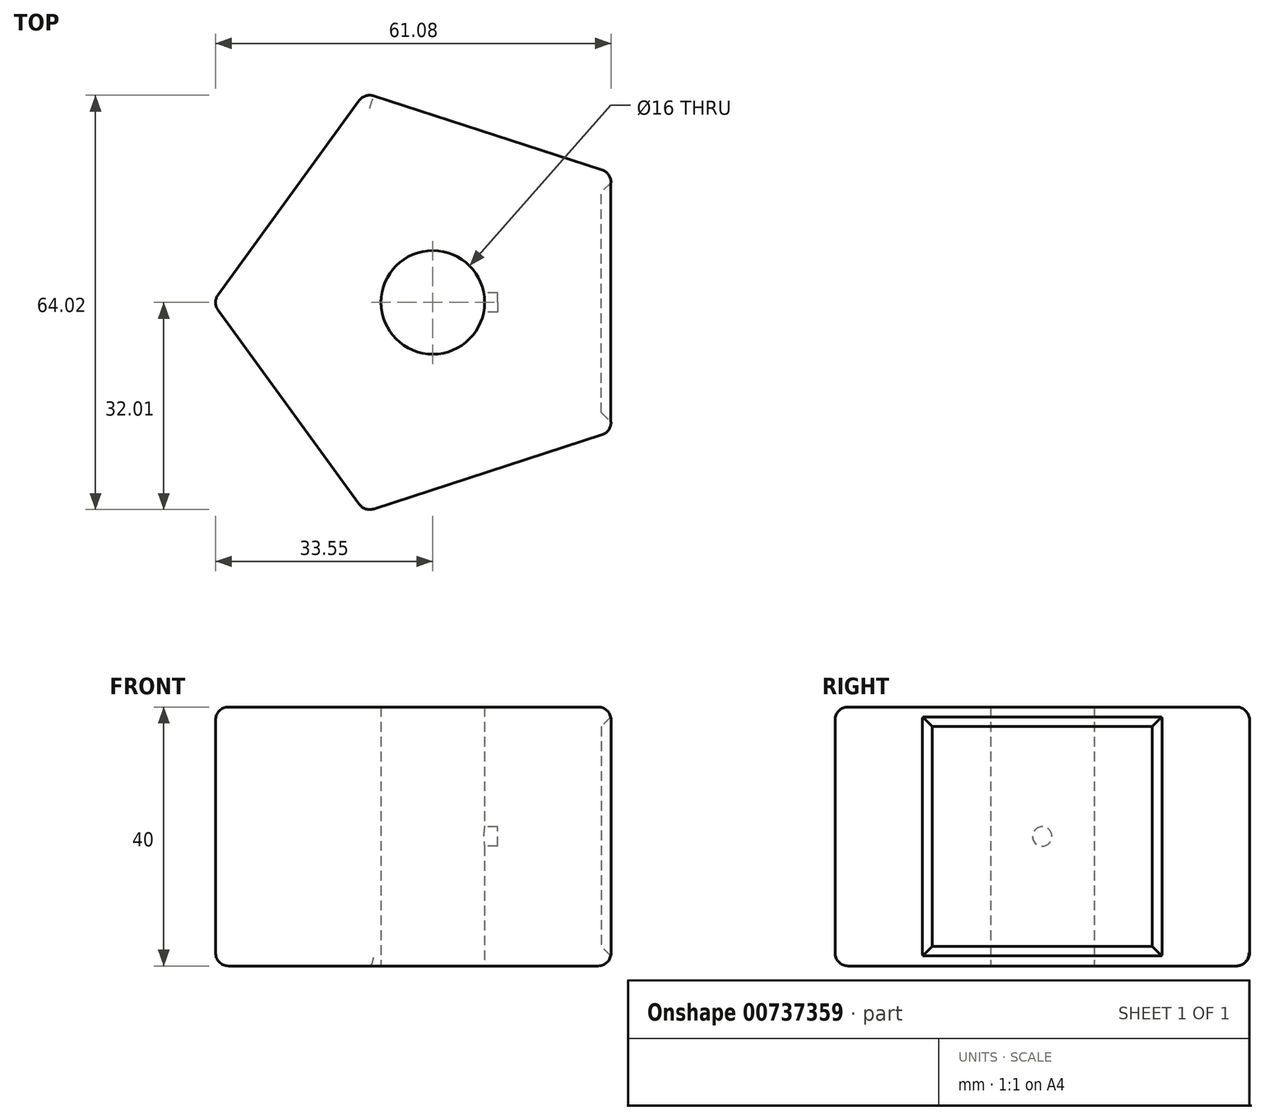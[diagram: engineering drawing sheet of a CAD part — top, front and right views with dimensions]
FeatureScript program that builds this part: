
annotation { "Feature Type Name" : "Feature", "Feature Type Description" : "" }
export const myFeature = defineFeature(function(context is Context, id is Id, definition is map)
    precondition{}
    {
        {
            var Q0;
            Q0=qCreatedBy(makeId("Top.planeOp"),FACE);
            var sketch = newSketch(context, id + "F0", { "sketchPlane" : qUnion([Q0])});
            skCircle(sketch, "E0.cCircle", {"center": v(0, 0) * mm, "radius": 27.53 * mm, "construction": true});
            skLineSegment(sketch, "E0.0", {"start": v(27.53, 20) * mm, "end": v(27.53, -20) * mm});
            skLineSegment(sketch, "E0.1", {"start": v(27.53, -20) * mm, "end": v(-10.51, -32.36) * mm});
            skLineSegment(sketch, "E0.2", {"start": v(-10.51, -32.36) * mm, "end": v(-34.03, 0) * mm});
            skLineSegment(sketch, "E0.3", {"start": v(-34.03, 0) * mm, "end": v(-10.51, 32.36) * mm});
            skLineSegment(sketch, "E0.4", {"start": v(-10.51, 32.36) * mm, "end": v(27.53, 20) * mm});
            skPoint(sketch, "E0.0.midPoint", {"position": v(27.53, 0) * mm});
            skCircle(sketch, "E1", {"center": v(0, 0) * mm, "radius": 8 * mm});
            skSolve(sketch);
        }
        {
            var Q0;
            Q0 = qSketchRegion(id + "F0", true);
            extrude(context, id + "F1", {"entities" : qUnion([Q0]), "depth" : 40 * mm, "offsetDistance" : 25 * mm});
        }
        {
            var Q0;
            Q0=makeQuery(id+"F1.opExtrude","SWEPT_FACE",FACE,{"disambiguationData":[OSD([sQuery(id+"F0.wireOp",EDGE,"E0.0")])]});
            var sketch = newSketch(context, id + "F2", { "sketchPlane" : qUnion([Q0])});
            skLineSegment(sketch, "E2.bottom", {"start": v(-18.5, 38.5) * mm, "end": v(18.5, 38.5) * mm});
            skLineSegment(sketch, "E2.top", {"start": v(-18.5, 1.5) * mm, "end": v(18.5, 1.5) * mm});
            skLineSegment(sketch, "E2.left", {"start": v(-18.5, 38.5) * mm, "end": v(-18.5, 1.5) * mm});
            skLineSegment(sketch, "E2.right", {"start": v(18.5, 38.5) * mm, "end": v(18.5, 1.5) * mm});
            skSolve(sketch);
        }
        {
            var Q0;
            Q0 = qSketchRegion(id + "F2", true);
            extrude(context, id + "F3", {"entities" : qUnion([Q0]), "operationType" : NewBodyOperationType.REMOVE, "oppositeDirection" : true, "depth" : 1.5 * mm, "offsetDistance" : 25 * mm});
        }
        {
            var Q0;
            Q0=makeQuery(id+"F3.boolean.opBoolean","COPY",FACE,{"derivedFrom":makeQuery(id+"F3.opExtrude","CAP_FACE",FACE,{"disambiguationData":[OSD([sQuery(id+"F2.wireOp",EDGE,"E2.bottom"),sQuery(id+"F2.wireOp",EDGE,"E2.top"),sQuery(id+"F2.wireOp",EDGE,"E2.left"),sQuery(id+"F2.wireOp",EDGE,"E2.right")])],"isStart":false})});
            var Q1;
            Q1=makeQuery(id+"FQoVGiJOBUNMoMP_1.-4.F3.boolean.opBoolean","COPY",FACE,{"derivedFrom":makeQuery(id+"FQoVGiJOBUNMoMP_1.-4.F3.opExtrude","CAP_FACE",FACE,{"disambiguationData":[OSD([sQuery(id+"F2.wireOp",EDGE,"E2.bottom"),sQuery(id+"F2.wireOp",EDGE,"E2.top"),sQuery(id+"F2.wireOp",EDGE,"E2.left"),sQuery(id+"F2.wireOp",EDGE,"E2.right")])],"isStart":false})});
            var Q2;
            Q2=makeQuery(id+"FQoVGiJOBUNMoMP_1.-3.F3.boolean.opBoolean","COPY",FACE,{"derivedFrom":makeQuery(id+"FQoVGiJOBUNMoMP_1.-3.F3.opExtrude","CAP_FACE",FACE,{"disambiguationData":[OSD([sQuery(id+"F2.wireOp",EDGE,"E2.bottom"),sQuery(id+"F2.wireOp",EDGE,"E2.top"),sQuery(id+"F2.wireOp",EDGE,"E2.left"),sQuery(id+"F2.wireOp",EDGE,"E2.right")])],"isStart":false})});
            var Q3;
            Q3=makeQuery(id+"FQoVGiJOBUNMoMP_1.-2.F3.boolean.opBoolean","COPY",FACE,{"derivedFrom":makeQuery(id+"FQoVGiJOBUNMoMP_1.-2.F3.opExtrude","CAP_FACE",FACE,{"disambiguationData":[OSD([sQuery(id+"F2.wireOp",EDGE,"E2.bottom"),sQuery(id+"F2.wireOp",EDGE,"E2.top"),sQuery(id+"F2.wireOp",EDGE,"E2.left"),sQuery(id+"F2.wireOp",EDGE,"E2.right")])],"isStart":false})});
            var Q4;
            Q4=makeQuery(id+"FQoVGiJOBUNMoMP_1.-1.F3.boolean.opBoolean","COPY",FACE,{"derivedFrom":makeQuery(id+"FQoVGiJOBUNMoMP_1.-1.F3.opExtrude","CAP_FACE",FACE,{"disambiguationData":[OSD([sQuery(id+"F2.wireOp",EDGE,"E2.bottom"),sQuery(id+"F2.wireOp",EDGE,"E2.top"),sQuery(id+"F2.wireOp",EDGE,"E2.left"),sQuery(id+"F2.wireOp",EDGE,"E2.right")])],"isStart":false})});
            chamfer(context, id + "F4", {"entities" : qUnion([Q0, Q1, Q2, Q3, Q4]), "width" : 1.5 * mm, "tangentPropagation" : true});
        }
        {
            var Q0;
            Q0=qCreatedBy(makeId("Right.planeOp"),FACE);
            var sketch = newSketch(context, id + "F5", { "sketchPlane" : qUnion([Q0])});
            skCircle(sketch, "E3", {"center": v(0, 49.5) * mm, "radius": 3 * mm});
            skSolve(sketch);
        }
        {
            var Q0;
            Q0 = qSketchRegion(id + "F5", true);
            extrude(context, id + "F6", {"entities" : qUnion([Q0]), "operationType" : NewBodyOperationType.REMOVE, "depth" : 20 * mm, "offsetDistance" : 25 * mm});
        }
        {
            var Q0;
            Q0=makeQuery(id+"F1.opExtrude","SWEPT_EDGE",EDGE,{"disambiguationData":[OSD([sQuery(id+"F0.wireOp",EDGE,"E0.2"),sQuery(id+"F0.wireOp",EDGE,"E0.3")])]});
            var Q1;
            Q1=makeQuery(id+"F1.opExtrude","SWEPT_EDGE",EDGE,{"disambiguationData":[OSD([sQuery(id+"F0.wireOp",EDGE,"E0.1"),sQuery(id+"F0.wireOp",EDGE,"E0.2")])]});
            var Q2;
            Q2=makeQuery(id+"F1.opExtrude","SWEPT_EDGE",EDGE,{"disambiguationData":[OSD([sQuery(id+"F0.wireOp",EDGE,"E0.0"),sQuery(id+"F0.wireOp",EDGE,"E0.1")])]});
            var Q3;
            Q3=makeQuery(id+"F1.opExtrude","SWEPT_EDGE",EDGE,{"disambiguationData":[OSD([sQuery(id+"F0.wireOp",EDGE,"E0.0"),sQuery(id+"F0.wireOp",EDGE,"E0.4")])]});
            var Q4;
            Q4=makeQuery(id+"F1.opExtrude","SWEPT_EDGE",EDGE,{"disambiguationData":[OSD([sQuery(id+"F0.wireOp",EDGE,"E0.3"),sQuery(id+"F0.wireOp",EDGE,"E0.4")])]});
            fillet(context, id + "F7", {"entities" : qUnion([Q0, Q1, Q2, Q3, Q4]), "radius" : 2 * mm, "tangentPropagation" : true, "allowEdgeOverflow" : false});
        }
        {
            var Q0;
            Q0=makeQuery(id+"F1.opExtrude","CAP_EDGE",EDGE,{"disambiguationData":[OSD([sQuery(id+"F0.wireOp",EDGE,"E0.1")])],"isStart":false});
            var Q1;
            Q1=makeQuery(id+"F1.opExtrude","CAP_EDGE",EDGE,{"disambiguationData":[OSD([sQuery(id+"F0.wireOp",EDGE,"E0.1")])],"isStart":true});
            fillet(context, id + "F8", {"entities" : qUnion([Q0, Q1]), "radius" : 2 * mm, "tangentPropagation" : true, "allowEdgeOverflow" : false});
        }
        {
            var Q0;
            Q0=qCreatedBy(makeId("Right.planeOp"),FACE);
            var sketch = newSketch(context, id + "F9", { "sketchPlane" : qUnion([Q0])});
            skCircle(sketch, "E4", {"center": v(0, 20) * mm, "radius": 1.5 * mm});
            skSolve(sketch);
        }
        {
            var Q0;
            Q0 = qSketchRegion(id + "F9", true);
            extrude(context, id + "F10", {"entities" : qUnion([Q0]), "operationType" : NewBodyOperationType.REMOVE, "depth" : 10 * mm, "offsetDistance" : 25 * mm});
        }
    });
